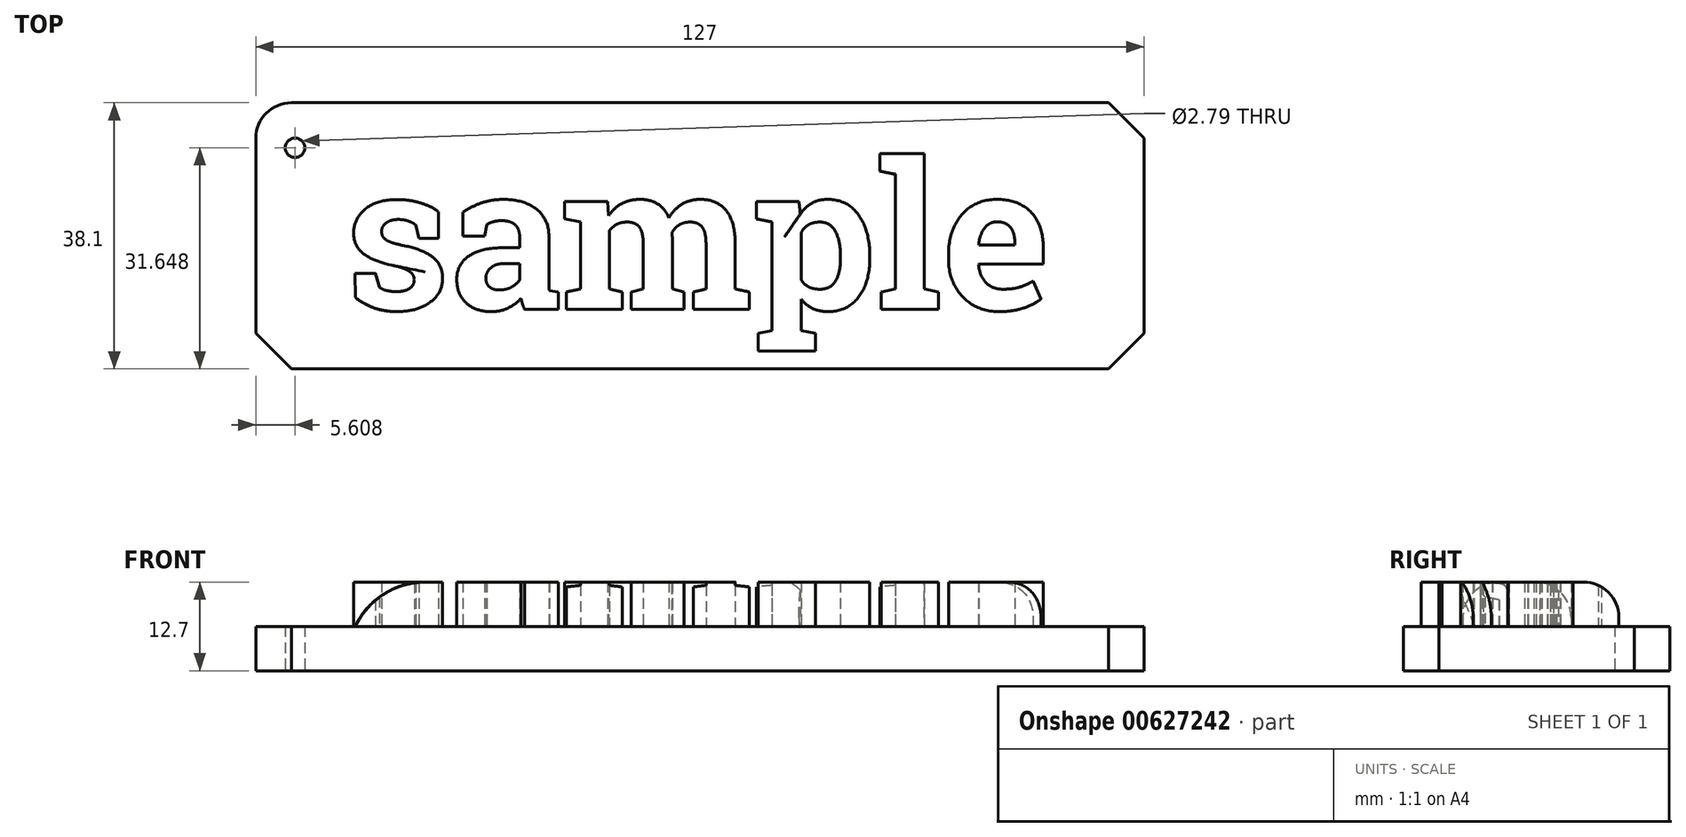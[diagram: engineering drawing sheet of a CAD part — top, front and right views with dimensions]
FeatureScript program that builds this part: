
annotation { "Feature Type Name" : "Feature", "Feature Type Description" : "" }
export const myFeature = defineFeature(function(context is Context, id is Id, definition is map)
    precondition{}
    {
        {
            var Q0;
            Q0=qCreatedBy(makeId("Top.planeOp"),FACE);
            var sketch = newSketch(context, id + "F0", { "sketchPlane" : qUnion([Q0])});
            skText(sketch, "E0", { "text": "sample", "fontName": "RobotoSlab-Bold.ttf"});
            const initialGuessF0  = {"E0": [-0.0509, -0.01054, 1, 0, 0.02109]};
            skSetInitialGuess(sketch, initialGuessF0);
            skSolve(sketch);
        }
        {
            var Q0;
            Q0=qCreatedBy(makeId("Top.planeOp"),FACE);
            var sketch = newSketch(context, id + "F1", { "sketchPlane" : qUnion([Q0])});
            skLineSegment(sketch, "E1.bottom", {"start": v(63.5, 19.05) * mm, "end": v(-63.5, 19.05) * mm});
            skLineSegment(sketch, "E1.top", {"start": v(63.5, -19.05) * mm, "end": v(-63.5, -19.05) * mm});
            skLineSegment(sketch, "E1.left", {"start": v(63.5, 19.05) * mm, "end": v(63.5, -19.05) * mm});
            skLineSegment(sketch, "E1.right", {"start": v(-63.5, 19.05) * mm, "end": v(-63.5, -19.05) * mm});
            skLineSegment(sketch, "E2.bottom", {"start": v(63.5, -19.05) * mm, "end": v(63.5, -19.05) * mm});
            skLineSegment(sketch, "E2.top", {"start": v(63.5, -1.62) * mm, "end": v(63.5, -1.62) * mm});
            skLineSegment(sketch, "E2.left", {"start": v(63.5, -19.05) * mm, "end": v(63.5, -1.62) * mm});
            skLineSegment(sketch, "E2.right", {"start": v(63.5, -19.05) * mm, "end": v(63.5, -1.62) * mm});
            skSolve(sketch);
        }
        {
            var Q0;
            Q0 = qSketchRegion(id + "F1", true);
            extrude(context, id + "F2", {"entities" : qUnion([Q0]), "depth" : 6.35 * mm, "offsetDistance" : 25.4 * mm});
        }
        {
            var Q0;
            Q0 = qSketchRegion(id + "F0", true);
            extrude(context, id + "F3", {"entities" : qUnion([Q0]), "operationType" : NewBodyOperationType.ADD, "depth" : 12.7 * mm, "offsetDistance" : 25.4 * mm});
        }
        {
            var Q0;
            Q0=makeQuery(id+"F2.opExtrude","SWEPT_EDGE",EDGE,{"disambiguationData":[OSD([sQuery(id+"F1.wireOp",EDGE,"E1.top"),sQuery(id+"F1.wireOp",EDGE,"E2.right")])]});
            var Q1;
            Q1=makeQuery(id+"F2.opExtrude","SWEPT_EDGE",EDGE,{"disambiguationData":[OSD([sQuery(id+"F1.wireOp",EDGE,"E1.bottom"),sQuery(id+"F1.wireOp",EDGE,"E1.left")])]});
            chamfer(context, id + "F4", {"entities" : qUnion([Q0, Q1]), "width" : 5.08 * mm, "tangentPropagation" : true});
        }
        {
            var Q0;
            Q0=makeQuery(id+"F2.opExtrude","SWEPT_EDGE",EDGE,{"disambiguationData":[OSD([sQuery(id+"F1.wireOp",EDGE,"E1.top"),sQuery(id+"F1.wireOp",EDGE,"E1.right")])]});
            var Q1;
            Q1=makeQuery(id+"F2.opExtrude","SWEPT_EDGE",EDGE,{"disambiguationData":[OSD([sQuery(id+"F1.wireOp",EDGE,"E1.bottom"),sQuery(id+"F1.wireOp",EDGE,"E1.right")])]});
            fillet(context, id + "F5", {"entities" : qUnion([Q0, Q1]), "radius" : 5.08 * mm, "tangentPropagation" : true, "allowEdgeOverflow" : false});
        }
        {
            var Q0;
            Q0=makeQuery(id+"F3.opExtrude","CAP_EDGE",EDGE,{"disambiguationData":[OSD([sQuery(id+"F0.wireOp",EDGE,"E0.sketch_text.stroke-103")])],"isStart":false});
            var Q1;
            Q1=makeQuery(id+"F3.opExtrude","CAP_EDGE",EDGE,{"disambiguationData":[OSD([sQuery(id+"F0.wireOp",EDGE,"E0.sketch_text.stroke-79")])],"isStart":false});
            var Q2;
            Q2=makeQuery(id+"F3.opExtrude","CAP_EDGE",EDGE,{"disambiguationData":[OSD([sQuery(id+"F0.wireOp",EDGE,"E0.sketch_text.stroke-139")])],"isStart":false});
            var Q3;
            Q3=makeQuery(id+"F3.opExtrude","CAP_EDGE",EDGE,{"disambiguationData":[OSD([sQuery(id+"F0.wireOp",EDGE,"E0.sketch_text.stroke-109")])],"isStart":false});
            fillet(context, id + "F6", {"entities" : qUnion([Q0, Q1, Q2, Q3]), "radius" : 5.08 * mm, "tangentPropagation" : true, "allowEdgeOverflow" : false});
        }
        {
            var Q0;
            Q0=makeQuery(id+"F3.opExtrude","CAP_EDGE",EDGE,{"disambiguationData":[OSD([sQuery(id+"F0.wireOp",EDGE,"E0.sketch_text.stroke-14")])],"isStart":false});
            fillet(context, id + "F7", {"entities" : qUnion([Q0]), "radius" : 11.04 * mm, "tangentPropagation" : true, "allowEdgeOverflow" : false});
        }
        {
            var Q0;
            Q0=makeQuery(id+"F3.opExtrude","CAP_EDGE",EDGE,{"disambiguationData":[OSD([sQuery(id+"F0.wireOp",EDGE,"E0.sketch_text.stroke-162")])],"isStart":false});
            fillet(context, id + "F8", {"entities" : qUnion([Q0]), "radius" : 5.08 * mm, "tangentPropagation" : true, "allowEdgeOverflow" : false});
        }
        {
            var Q0;
            Q0=qCreatedBy(makeId("Top.planeOp"),FACE);
            var sketch = newSketch(context, id + "F9", { "sketchPlane" : qUnion([Q0])});
            skPoint(sketch, "E3", {"position": v(-57.9, 12.6) * mm});
            skSolve(sketch);
        }
        {
            var Q0;
            Q0=sQuery(id+"F9.wireOp",VERTEX,"E3");
            var Q1;
            Q1=makeQuery(id+"F2.opExtrude","SWEPT_BODY",BODY,{"disambiguationData":[OSD([sQuery(id+"F1.wireOp",EDGE,"E1.bottom"),sQuery(id+"F1.wireOp",EDGE,"E1.top"),sQuery(id+"F1.wireOp",EDGE,"E1.left"),sQuery(id+"F1.wireOp",EDGE,"E1.right"),sQuery(id+"F1.wireOp",EDGE,"E2.right")])]});
            hole(context, id + "F10", {"style" : HoleStyle.SIMPLE, "endStyle" : HoleEndStyle.THROUGH, "oppositeDirection" : true, "standardTappedOrClearance" : lookupTablePath({ "standard" : "ANSI", "fit" : "Normal (ASME)", "size" : "#3", "type" : "Clearance" }), "standardBlindInLast" : lookupTablePath({ "fit" : "Free", "standard" : "ANSI", "size" : "#3", "type" : "Clearance" }), "holeDiameter" : 2.8 * mm, "majorDiameter" : 6.35 * mm, "isTappedThrough" : true, "tappedDepth" : 12.7 * mm, "tapClearance" : 3, "locations" : qUnion([Q0]), "scope" : qUnion([Q1])});
        }
    });
